# Revit family: Gira_2003100
name_source: partatom
category: Electrical Fixtures
revit_build: Autodesk Revit 2017 (Build: 20160225_1515(x64)
units: mm (PartAtom-declared; Revit-internal decimal feet)

## family parameters
Cut with Voids When Loaded = No
Host = Face
Maintain Annotation Orientation = Yes
Part Type = Normal
Room Calculation Point = No
Round Connector Dimension = Use Diameter
Shared = No

## types (1)
- PB sens.2 3-g 24 V zero-volt. in.sp. System 55 clear/p.white
    Available = No
    BIM (1) = https://media.stage.bim.site und Tasten.rfa?public/gira/36a6b08/Sys55_Komplettgerät_Schalten und Tasten.rfa
    Bus connection included = No
    Bus system KNX = Yes
    Bus system KNX radio = No
    Bus system LON = No
    Bus system Powernet = No
    Bus system radio frequent = Yes
    Category = Touch sensor for bus system
    Data sheet (1) = https://katalog.gira.de
    Default Elevation = 1219 mm
    Description = PB sens 2 3g 24V z-v Sys55 ClPw,Pushbutton sensor 2, 3-gang 24 V zero-voltage with inscription space,,clear + pure white glossy,Features:,Pushbutton sensor 2 for connection to 24 V control systems:,- Three rockers with two red LEDs each for status display.,- Disassembly safeguard by screw connection.,- Backlighting.,- Connection of six buttons, six LEDs, and backlighting via the terminal block on the rear.,,Notes :,- Suitable for SELV circuits only.,- Can also be connected with illumination.,- Professional labelling with the Gira Inscription Service www.marking.gira.com.
    GTIN = 4010337047971
    HAN = 2003100
    HeinzeBIM = https://bimportal.heinze.de
    Manufacturer = Gira
    Manufacturer URL = https://www.gira.de
    Model = Sys55_Komplettgerät_Schalten und Tasten
    Name = PB sens.2 3-g 24 V zero-volt. in.sp. System 55 clear/p.white
    Number of actuation points = 6
    Number of buttons = 3
    Other bus systems = None
    Transparent = Yes
    URL = http://katalog.gira.de
    With IR sensor = No
    With LED indication = Yes
    With anti-theft/dismantling protection = No
    With room temperature controller = No

## geometry (parser evidence)
native form markers: Blend x2, Sweep x11
no freeform markers — native parametric forms only
